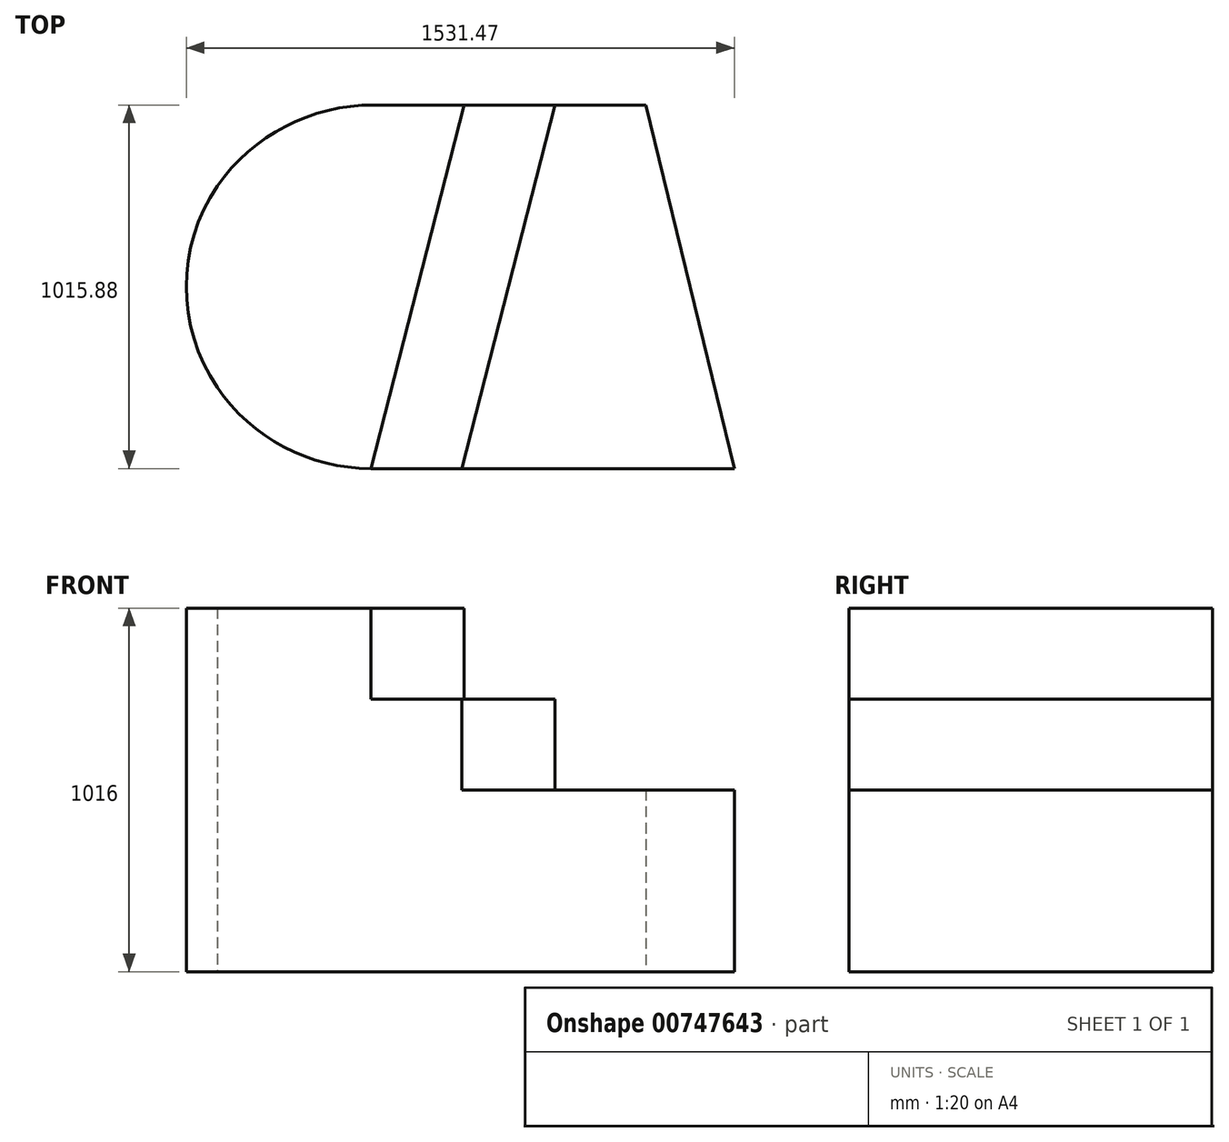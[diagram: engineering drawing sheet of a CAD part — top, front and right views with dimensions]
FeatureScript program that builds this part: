
annotation { "Feature Type Name" : "Feature", "Feature Type Description" : "" }
export const myFeature = defineFeature(function(context is Context, id is Id, definition is map)
    precondition{}
    {
        {
            var Q0;
            Q0=qCreatedBy(makeId("Top.planeOp"),FACE);
            var sketch = newSketch(context, id + "F0", { "sketchPlane" : qUnion([Q0])});
            skLineSegment(sketch, "E0.bottom", {"start": v(0, 513.13) * mm, "end": v(762, 513.13) * mm});
            skLineSegment(sketch, "E0.top", {"start": v(-7.3, -502.73) * mm, "end": v(754.7, -502.73) * mm});
            skLineSegment(sketch, "E1", {"start": v(754.7, -502.73) * mm, "end": v(1008.7, -502.75) * mm});
            skLineSegment(sketch, "E2", {"start": v(762, 513.13) * mm, "end": v(1008.7, -502.75) * mm});
            skArc(sketch, "E3", {"start": v(0, 513.13) * mm, "mid": v(-246.02, 453.02) * mm, "end": v(-436.61, 286.24) * mm});
            skArc(sketch, "E4", {"start": v(-436.61, 286.24) * mm, "mid": v(-522.76, 5.3) * mm, "end": v(-436.61, -275.63) * mm});
            skArc(sketch, "E5", {"start": v(-436.61, -275.63) * mm, "mid": v(-250.14, -442.46) * mm, "end": v(-7.3, -502.73) * mm});
            skSolve(sketch);
        }
        {
            var Q0;
            Q0 = qSketchRegion(id + "F0", true);
            extrude(context, id + "F1", {"entities" : qUnion([Q0]), "depth" : 1016 * mm, "offsetDistance" : 25 * mm});
        }
        {
            var Q0;
            Q0=makeQuery(id+"F1.opExtrude","CAP_FACE",FACE,{"disambiguationData":[OSD([sQuery(id+"F0.wireOp",EDGE,"E0.bottom"),sQuery(id+"F0.wireOp",EDGE,"E0.top"),sQuery(id+"F0.wireOp",EDGE,"E1"),sQuery(id+"F0.wireOp",EDGE,"E2"),sQuery(id+"F0.wireOp",EDGE,"E3"),sQuery(id+"F0.wireOp",EDGE,"E4"),sQuery(id+"F0.wireOp",EDGE,"E5")])],"isStart":false});
            var sketch = newSketch(context, id + "F2", { "sketchPlane" : qUnion([Q0])});
            skLineSegment(sketch, "E6", {"start": v(-7.3, -502.73) * mm, "end": v(254, 513.13) * mm});
            skLineSegment(sketch, "E7", {"start": v(508, 513.13) * mm, "end": v(246.7, -502.73) * mm});
            skSolve(sketch);
        }
        {
            var Q0;
            {var subQ0=sQuery(id+"F2.wireOp",EDGE,"E6");Q0=makeQuery(id+"F2.imprint","IMPRINT",FACE,{"disambiguationData":[TD([[makeQuery(id+"F2.imprint","IMPRINT",EDGE,{"derivedFrom":subQ0}),-1.0]])]});}
            extrude(context, id + "F3", {"entities" : qUnion([Q0]), "operationType" : NewBodyOperationType.REMOVE, "oppositeDirection" : true, "depth" : 254 * mm, "offsetDistance" : 25 * mm});
        }
        {
            var Q0;
            {var subQ0=sQuery(id+"F0.wireOp",EDGE,"E1");var subQ1=sQuery(id+"F0.wireOp",EDGE,"E0.top");var subQ2=sQuery(id+"F0.wireOp",EDGE,"E2");var subQ3=sQuery(id+"F0.wireOp",EDGE,"E0.bottom");Q0=makeQuery(id+"F3.boolean.opBoolean","SPLIT",FACE,{"disambiguationData":[TD([makeQuery(id+"F1.opExtrude","SWEPT_FACE",FACE,{"disambiguationData":[OSD([subQ1])]})])],"derivedFrom":makeQuery(id+"F1.opExtrude","CAP_FACE",FACE,{"disambiguationData":[OSD([subQ3,subQ1,subQ0,subQ2,sQuery(id+"F0.wireOp",EDGE,"E3"),sQuery(id+"F0.wireOp",EDGE,"E4"),sQuery(id+"F0.wireOp",EDGE,"E5")])],"isStart":false})});}
            var sketch = newSketch(context, id + "F4", { "sketchPlane" : qUnion([Q0])});
            skSolve(sketch);
        }
        {
            var Q0;
            {var subQ3=sQuery(id+"F0.wireOp",EDGE,"E1");Q0=makeQuery(id+"F4.imprint","IMPRINT",FACE,{"disambiguationData":[TD([[makeQuery(id+"F4.imprint","IMPRINT",EDGE,{"derivedFrom":makeQuery(id+"F1.opExtrude","CAP_EDGE",EDGE,{"disambiguationData":[OSD([subQ3])],"isStart":false})}),1.0]])]});}
            var sketch = newSketch(context, id + "F5", { "sketchPlane" : qUnion([Q0])});
            skSolve(sketch);
        }
        {
            var Q0;
            Q0 = qSketchRegion(id + "F5", true);
            var Q1;
            {var subQ3=sQuery(id+"F0.wireOp",EDGE,"E1");Q1=makeQuery(id+"F4.imprint","IMPRINT",FACE,{"disambiguationData":[TD([[makeQuery(id+"F4.imprint","IMPRINT",EDGE,{"derivedFrom":makeQuery(id+"F1.opExtrude","CAP_EDGE",EDGE,{"disambiguationData":[OSD([subQ3])],"isStart":false})}),1.0]])]});}
            extrude(context, id + "F6", {"entities" : qUnion([Q0, Q1]), "operationType" : NewBodyOperationType.REMOVE, "oppositeDirection" : true, "depth" : 508 * mm, "offsetDistance" : 25 * mm});
        }
        {
            var Q0;
            {var subQ3=sQuery(id+"F0.wireOp",EDGE,"E1");Q0=makeQuery(id+"F5.imprint","IMPRINT",FACE,{"disambiguationData":[TD([[makeQuery(id+"F5.imprint","IMPRINT",EDGE,{"derivedFrom":makeQuery(id+"F4.imprint","IMPRINT",EDGE,{"derivedFrom":makeQuery(id+"F1.opExtrude","CAP_EDGE",EDGE,{"disambiguationData":[OSD([subQ3])],"isStart":false})})}),1.0]])]});}
            extrude(context, id + "F7", {"entities" : qUnion([Q0]), "depth" : 25 * mm, "offsetDistance" : 25 * mm});
        }
        {
            var Q0;
            Q0=makeQuery(id+"F7.opExtrude","CAP_FACE",FACE,{"disambiguationData":[OSD([sQuery(id+"F0.wireOp",EDGE,"E0.bottom"),sQuery(id+"F0.wireOp",EDGE,"E0.top"),sQuery(id+"F0.wireOp",EDGE,"E1"),sQuery(id+"F0.wireOp",EDGE,"E2"),sQuery(id+"F2.wireOp",EDGE,"E7")])],"isStart":false});
            extrude(context, id + "F8", {"entities" : qUnion([Q0]), "operationType" : NewBodyOperationType.REMOVE, "oppositeDirection" : true, "depth" : 100 * mm, "offsetDistance" : 25 * mm});
        }
    });
